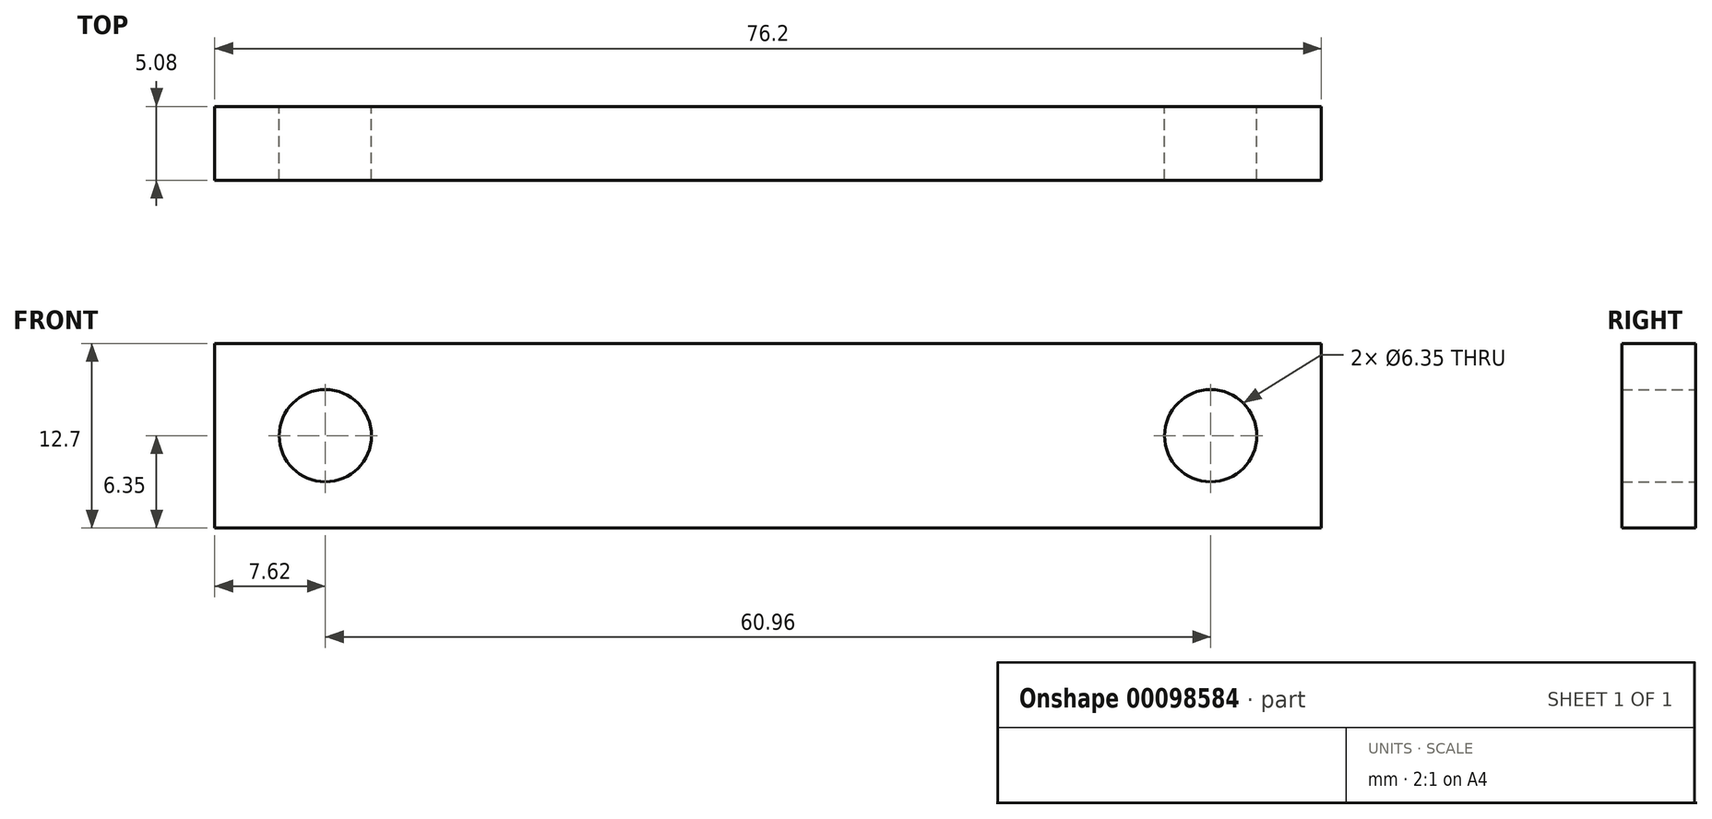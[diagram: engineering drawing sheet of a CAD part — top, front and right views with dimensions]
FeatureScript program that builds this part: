
annotation { "Feature Type Name" : "Feature", "Feature Type Description" : "" }
export const myFeature = defineFeature(function(context is Context, id is Id, definition is map)
    precondition{}
    {
        {
            var Q0;
            Q0=qCreatedBy(makeId("Front.planeOp"),FACE);
            var sketch = newSketch(context, id + "F0", { "sketchPlane" : qUnion([Q0])});
            skLineSegment(sketch, "E0.bottom", {"start": v(-38.1, 6.35) * mm, "end": v(38.1, 6.35) * mm});
            skLineSegment(sketch, "E0.top", {"start": v(-38.1, -6.35) * mm, "end": v(38.1, -6.35) * mm});
            skLineSegment(sketch, "E0.left", {"start": v(-38.1, 6.35) * mm, "end": v(-38.1, -6.35) * mm});
            skLineSegment(sketch, "E0.right", {"start": v(38.1, 6.35) * mm, "end": v(38.1, -6.35) * mm});
            skCircle(sketch, "E1", {"center": v(-30.48, 0) * mm, "radius": 3.18 * mm});
            skPoint(sketch, "E1.centerSnap0", {"position": v(-38.1, 0) * mm});
            skCircle(sketch, "E2", {"center": v(30.48, 0) * mm, "radius": 3.18 * mm});
            skPoint(sketch, "E3", {"position": v(38.1, 0) * mm});
            skSolve(sketch);
        }
        {
            var Q0;
            Q0 = qSketchRegion(id + "F0", true);
            var Q1;
            Q1=makeQuery(id+"F0.imprint","IMPRINT",FACE,{"disambiguationData":[TD([[makeQuery(id+"F0.imprint","IMPRINT",EDGE,{"derivedFrom":sQuery(id+"F0.wireOp",EDGE,"E0.bottom")}),-1.0]])]});
            extrude(context, id + "F1", {"entities" : qUnion([Q0, Q1]), "depth" : 5.08 * mm});
        }
    });
